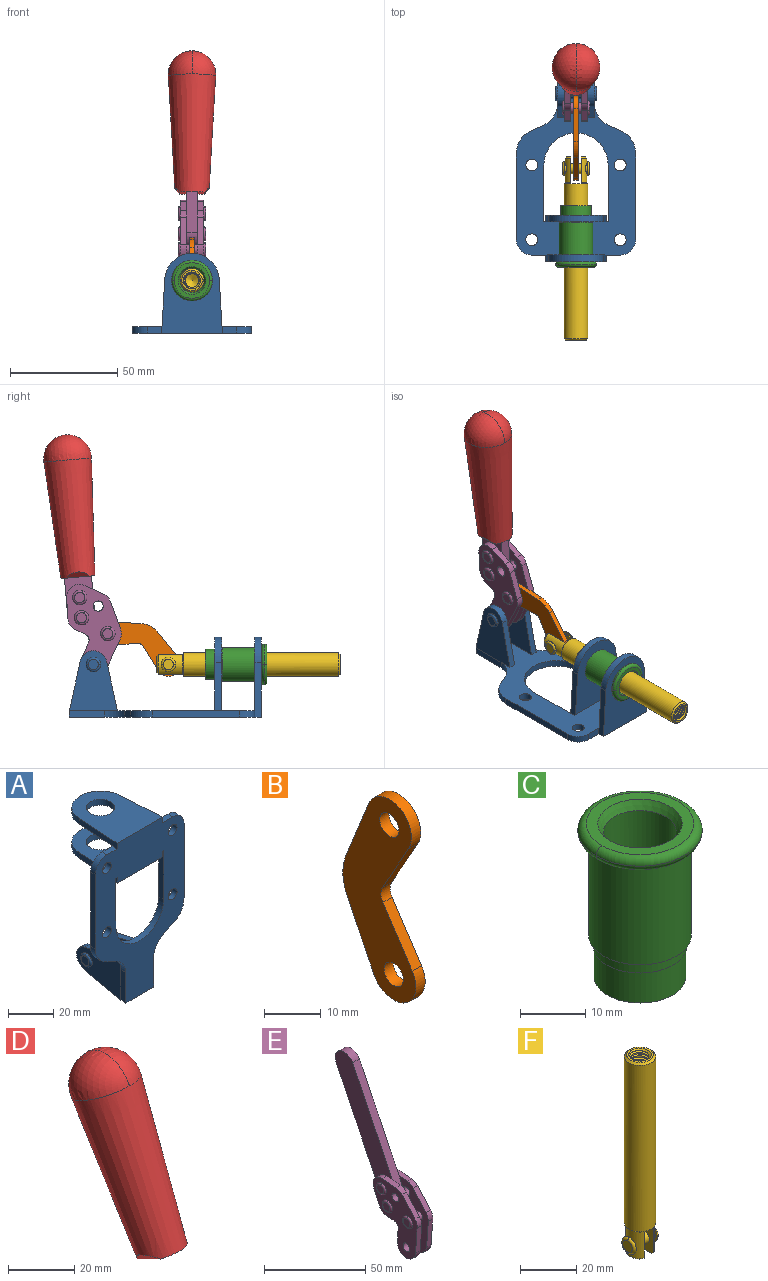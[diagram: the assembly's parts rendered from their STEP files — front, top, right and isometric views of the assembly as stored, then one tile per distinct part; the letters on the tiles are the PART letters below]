
ASSEMBLY  parts=6 mates=6
PART A: 55 faces, bbox 55.7x37.4x89.8 mm
  f0: torus R=2.41mm, axis (-1,0,0), area 15mm2, adj f11,f15,f25
  f1: torus R=2.41mm, axis (-1,0,0), area 15mm2, adj f10,f12,f22
  f2: cylinder r=2.78mm len=5.56mm, axis (0,-1,0), area 54.2mm2, adj f30,f54
  f3: cylinder r=14.99mm len=29.97mm, axis (0,-1,0), area 145.9mm2, adj f30,f49,f53,f54
  f4: cylinder r=2.78mm len=5.56mm, axis (0,-1,0), area 54.2mm2, adj f30,f54
  f5: cylinder r=2.78mm len=5.56mm, axis (0,-1,0), area 54.2mm2, adj f30,f54
  f6: cylinder r=2.78mm len=5.56mm, axis (0,-1,0), area 54.2mm2, adj f30,f54
  f7: cylinder r=6.35mm len=12.7mm, axis (0,0,1), area 123.6mm2, adj f27,f51
  f8: cylinder r=6.35mm len=12.7mm, axis (0,0,-1), area 124.7mm2, adj f21,f35
  f9: cylinder r=2.41mm len=11.18mm, axis (-1,0,0), area 169.4mm2, adj f16,f19
  f10: plane 4.83x4.83mm, normal (1,0,0), area 18.3mm2, adj f1,f12
  f11: plane 4.83x4.83mm, normal (-1,0,0), area 18.3mm2, adj f0,f15
  f12: torus R=2.41mm, axis (-1,0,0), area 15mm2, adj f1,f10,f22
  f13: cylinder r=6.35mm len=12.41mm, axis (1,0,0), area 53.4mm2, adj f18,f19,f22,f23
  f14: cylinder r=6.35mm len=12.41mm, axis (-1,0,0), area 53.4mm2, adj f16,f17,f24,f25
  f15: torus R=2.41mm, axis (-1,0,0), area 15mm2, adj f0,f11,f25
  f16: plane 27.86x22.35mm, normal (1,0,0), area 425.4mm2, adj f9,f14,f17,f24,f30
  f17: plane 22.86x4.97mm, normal (0,0.21,0.98), area 72.5mm2, adj f14,f16,f25,f30
  f18: plane 22.86x4.97mm, normal (0,0.21,0.98), area 72.5mm2, adj f13,f19,f22,f30
  f19: plane 27.86x22.35mm, normal (-1,0,0), area 425.4mm2, adj f9,f13,f18,f23,f30
  f20: cylinder r=12.7mm len=25.35mm, axis (0,0,-1), area 119.8mm2, adj f21,f34,f35,f36
  f21: plane 34.21x28.07mm, normal (0,0,-1), area 702.4mm2, adj f8,f20,f30,f34,f36
  f22: plane 27.96x22.45mm, normal (1,0,0), area 407.2mm2, adj f1,f12,f13,f18,f23,f30,f42,f43
  f23: plane 22.86x4.97mm, normal (0,0.21,-0.98), area 72.5mm2, adj f13,f19,f22,f44
  f24: plane 22.86x4.97mm, normal (0,0.21,-0.98), area 72.5mm2, adj f14,f16,f25,f44
  f25: plane 27.86x22.35mm, normal (-1,0,0), area 407.1mm2, adj f0,f14,f15,f17,f24,f30,f45,f46
  f26: plane 3.1x0.95mm, normal (0,0,-1), area 2.7mm2, adj f30,f49,f50,f54
  f27: plane 34.21x28.07mm, normal (0,0,1), area 702.4mm2, adj f7,f28,f30,f50,f52
  f28: cylinder r=12.7mm len=25.35mm, axis (0,0,1), area 118.8mm2, adj f27,f50,f51,f52
  f29: plane 3.1x0.95mm, normal (0,0,-1), area 2.7mm2, adj f30,f52,f53,f54
  f30: plane 86.54x55.63mm, normal (0,1,0), area 2362.9mm2, adj f2,f3,f4,f5,f6,f16,f17,f18
  f31: plane 40.56x3.1mm, normal (-1,0,0), area 125.7mm2, adj f30,f32,f48,f54
  f32: cylinder r=7.11mm len=7.11mm, axis (0,-1,0), area 34.6mm2, adj f30,f31,f33,f54
  f33: plane 6.67x3.1mm, normal (0,0,1), area 20.4mm2, adj f30,f32,f34,f54
  f34: plane 25.39x3.13mm, normal (-1,0.06,0), area 79.5mm2, adj f20,f21,f33,f35,f54
  f35: plane 37.31x28.45mm, normal (0,0,1), area 789.9mm2, adj f8,f20,f34,f36,f54
  f36: plane 25.39x3.13mm, normal (1,0.06,0), area 79.5mm2, adj f20,f21,f35,f37,f54
  f37: plane 6.67x3.1mm, normal (0,0,1), area 20.4mm2, adj f30,f36,f38,f54
  f38: cylinder r=7.11mm len=7.11mm, axis (0,-1,0), area 34.6mm2, adj f30,f37,f39,f54
  f39: plane 40.56x3.1mm, normal (1,0,0), area 125.7mm2, adj f30,f38,f40,f54
  f40: cylinder r=11.18mm len=10.16mm, axis (0,-1,0), area 39.5mm2, adj f30,f39,f41,f54
  f41: plane 6.09x3.1mm, normal (0.42,0,-0.91), area 20.8mm2, adj f30,f40,f42,f54
  f42: cylinder r=11.18mm len=9.41mm, axis (0,-1,0), area 37.2mm2, adj f22,f30,f41,f43,f54
  f43: plane 16.5x3.1mm, normal (1,0,0), area 51.1mm2, adj f22,f42,f44,f54
  f44: plane 17.37x3.1mm, normal (0,0,-1), area 53.8mm2, adj f23,f24,f30,f43,f45,f54
  f45: plane 16.5x3.1mm, normal (-1,0,0), area 51.1mm2, adj f25,f44,f46,f54
  f46: cylinder r=11.18mm len=9.41mm, axis (0,-1,0), area 37.2mm2, adj f25,f30,f45,f47,f54
  f47: plane 6.09x3.1mm, normal (-0.42,0,-0.91), area 20.8mm2, adj f30,f46,f48,f54
  f48: cylinder r=11.18mm len=10.16mm, axis (0,-1,0), area 39.5mm2, adj f30,f31,f47,f54
  f49: plane 26.54x3.1mm, normal (-1,0,0), area 82.3mm2, adj f3,f26,f30,f54
  f50: plane 25.39x3.1mm, normal (1,0.06,0), area 78.8mm2, adj f26,f27,f28,f51,f54
  f51: plane 37.31x28.45mm, normal (0,0,-1), area 789.9mm2, adj f7,f28,f50,f52,f54
  f52: plane 25.39x3.1mm, normal (-1,0.06,0), area 78.8mm2, adj f27,f28,f29,f51,f54
  f53: plane 26.54x3.1mm, normal (1,0,0), area 82.3mm2, adj f3,f29,f30,f54
  f54: plane 89.66x55.63mm, normal (0,-1,0), area 2678.5mm2, adj f2,f3,f4,f5,f6,f26,f29,f31
PART B: 12 faces, bbox 2.3x18.2x42.8 mm
  f0: cylinder r=2.4mm len=4.8mm, axis (1,0,0), area 34.9mm2, adj f4,f11
  f1: cylinder r=10.41mm len=8.47mm, axis (1,0,0), area 20.2mm2, adj f4,f9,f10,f11
  f2: cylinder r=3.05mm len=3.16mm, axis (1,0,0), area 7.7mm2, adj f4,f6,f7,f11
  f3: cylinder r=2.4mm len=4.8mm, axis (1,0,0), area 34.9mm2, adj f4,f11
  f4: plane 42.81x18.23mm, normal (-1,0,0), area 414.1mm2, adj f0,f1,f2,f3,f5,f6,f7,f8
  f5: cylinder r=5.54mm len=10.67mm, axis (1,0,0), area 41.8mm2, adj f4,f6,f10,f11
  f6: plane 11.66x6.53mm, normal (0,-0.87,-0.49), area 30.9mm2, adj f2,f4,f5,f11
  f7: plane 11.17x7.33mm, normal (0,-0.84,0.55), area 30.9mm2, adj f2,f4,f8,f11
  f8: cylinder r=5.54mm len=10.51mm, axis (1,0,0), area 41.8mm2, adj f4,f7,f9,f11
  f9: plane 13.67x6.67mm, normal (0,0.9,-0.44), area 35.1mm2, adj f1,f4,f8,f11
  f10: plane 14.1x5.7mm, normal (0,0.93,0.37), area 35.1mm2, adj f1,f4,f5,f11
  f11: plane 42.81x18.23mm, normal (1,0,0), area 414.1mm2, adj f0,f1,f2,f3,f5,f6,f7,f8
PART C: 15 faces, bbox 20.6x20.6x28.7 mm
  f0: torus R=8.26mm, axis (0,0,1), area 56.8mm2, adj f1,f10,f12
  f1: torus R=8.26mm, axis (0,0,1), area 56.8mm2, adj f0,f6,f13
  f2: cylinder r=5.59mm len=25.91mm, axis (0,0,1), area 909.6mm2, adj f3,f4
  f3: cone r=6.86mm half-angle=45deg, axis (0,0,-1), area 70.2mm2, adj f2,f14
  f4: cone r=6.47mm half-angle=30deg, axis (0,0,1), area 66.7mm2, adj f2,f13
  f5: cylinder r=7.04mm len=14.07mm, axis (0,0,1), area 252.6mm2, adj f11,f14
  f6: torus R=8.26mm, axis (0,0,1), area 56.8mm2, adj f1,f12,f13
  f7: cylinder r=7.16mm len=14.33mm, axis (0,0,1), area 91.5mm2, adj f9,f11
  f8: cylinder r=7.86mm len=18.42mm, axis (0,0,1), area 909.6mm2, adj f9,f10
  f9: plane 15.72x15.72mm, normal (0,0,-1), area 33mm2, adj f7,f8
  f10: plane 16.51x16.51mm, normal (0,0,-1), area 19.9mm2, adj f0,f8,f12
  f11: plane 14.33x14.33mm, normal (0,0,-1), area 5.7mm2, adj f5,f7
  f12: torus R=8.26mm, axis (0,0,1), area 56.8mm2, adj f0,f6,f10
  f13: plane 16.51x16.51mm, normal (0,0,1), area 82.7mm2, adj f1,f4,f6
  f14: plane 14.07x14.07mm, normal (0,0,-1), area 7.8mm2, adj f3,f5
PART D: 11 faces, bbox 22.3x42.6x64.5 mm
  f0: sphere r=11.13mm, area 411.4mm2, adj f1,f8
  f1: cone r=11.11mm half-angle=3.3deg, axis (0,0.44,0.9), area 3251.8mm2, adj f0,f7,f8,f9,f10
  f2: cylinder r=6.16mm len=11.7mm, axis (1,0,0), area 89.5mm2, adj f3,f4,f5,f6
  f3: plane 60.23x36.75mm, normal (-1,0,0), area 763.6mm2, adj f2,f4,f6,f10
  f4: plane 51.37x25.05mm, normal (0,0.9,-0.44), area 264.2mm2, adj f2,f3,f5,f10
  f5: plane 60.23x36.75mm, normal (1,0,0), area 763.6mm2, adj f2,f4,f6,f10
  f6: plane 51.37x25.05mm, normal (0,-0.9,0.44), area 264.2mm2, adj f2,f3,f5,f10
  f7: plane 9.95x5.95mm, normal (0.71,-0.31,-0.64), area 25.8mm2, adj f1,f10
  f8: sphere r=11.13mm, area 411.4mm2, adj f0,f1
  f9: plane 9.95x5.95mm, normal (-0.71,-0.31,-0.64), area 25.8mm2, adj f1,f10
  f10: plane 14.27x11.38mm, normal (0,-0.44,-0.9), area 106.7mm2, adj f1,f3,f4,f5,f6,f7,f9
PART E: 59 faces, bbox 12.9x60.2x99.6 mm
  f0: torus R=2.39mm, axis (-1,0,0), area 14.9mm2, adj f20,f43,f51
  f1: torus R=2.39mm, axis (-1,0,0), area 14.9mm2, adj f19,f42,f51
  f2: torus R=2.39mm, axis (-1,0,0), area 14.9mm2, adj f18,f35,f51
  f3: torus R=2.39mm, axis (-1,0,0), area 14.9mm2, adj f14,f17,f23
  f4: torus R=2.39mm, axis (-1,0,0), area 14.9mm2, adj f13,f16,f23
  f5: torus R=2.39mm, axis (-1,0,0), area 14.9mm2, adj f12,f15,f23
  f6: cylinder r=2.39mm len=4.78mm, axis (1,0,0), area 46.5mm2, adj f48,f50,f51
  f7: cylinder r=2.39mm len=4.78mm, axis (1,0,0), area 46.5mm2, adj f50,f51
  f8: cylinder r=6.35mm len=12.68mm, axis (1,0,0), area 61.8mm2, adj f38,f39,f50,f51
  f9: cylinder r=2.39mm len=4.78mm, axis (-1,0,0), area 70.5mm2, adj f46,f50
  f10: cylinder r=2.39mm len=4.78mm, axis (-1,0,0), area 46.5mm2, adj f23,f45,f46
  f11: cylinder r=2.39mm len=4.78mm, axis (-1,0,0), area 46.5mm2, adj f23,f46
  f12: plane 4.78x4.78mm, normal (1,0,0), area 17.9mm2, adj f5,f15
  f13: plane 4.78x4.78mm, normal (1,0,0), area 17.9mm2, adj f4,f16
  f14: plane 4.78x4.78mm, normal (1,0,0), area 17.9mm2, adj f3,f17
  f15: torus R=2.39mm, axis (-1,0,0), area 14.9mm2, adj f5,f12,f23
  f16: torus R=2.39mm, axis (-1,0,0), area 14.9mm2, adj f4,f13,f23
  f17: torus R=2.39mm, axis (-1,0,0), area 14.9mm2, adj f3,f14,f23
  f18: plane 4.78x4.78mm, normal (-1,0,0), area 17.9mm2, adj f2,f35
  f19: plane 4.78x4.78mm, normal (-1,0,0), area 17.9mm2, adj f1,f42
  f20: plane 4.78x4.78mm, normal (-1,0,0), area 17.9mm2, adj f0,f43
  f21: plane 2.26x0.2mm, normal (1,0,0), area 0.2mm2, adj f31,f44
  f22: plane 2.26x0.2mm, normal (-1,0,0), area 0.2mm2, adj f41,f44
  f23: plane 39.37x30.77mm, normal (1,0,0), area 565.5mm2, adj f3,f4,f5,f10,f11,f15,f16,f17
  f24: cylinder r=6.1mm len=4.15mm, axis (-1,0,0), area 14.7mm2, adj f23,f25,f32,f46
  f25: plane 10.25x9.01mm, normal (0,-0.75,0.66), area 42.3mm2, adj f23,f24,f26,f46
  f26: cylinder r=6.35mm len=4.64mm, axis (-1,0,0), area 15.6mm2, adj f23,f25,f27,f46
  f27: plane 15.84x3.1mm, normal (0,-1,-0.07), area 49.2mm2, adj f23,f26,f28,f46
  f28: cylinder r=6.35mm len=12.68mm, axis (-1,0,0), area 61.8mm2, adj f23,f27,f29,f46
  f29: plane 8.11x3.1mm, normal (0,1,0.07), area 25.2mm2, adj f23,f28,f30,f46
  f30: cylinder r=3.05mm len=3.25mm, axis (-1,0,0), area 14.8mm2, adj f23,f29,f31,f46
  f31: plane 5.99x3.1mm, normal (0,0.07,-1), area 18.6mm2, adj f21,f23,f30,f44,f46
  f32: plane 9.5x3.1mm, normal (0,-0.07,1), area 29.5mm2, adj f23,f24,f33,f46,f47
  f33: cylinder r=6.1mm len=8.63mm, axis (-1,0,0), area 39.1mm2, adj f23,f32,f34,f47
  f34: plane 8.65x3.96mm, normal (0,0.91,-0.42), area 29.5mm2, adj f23,f33,f44,f47
  f35: torus R=2.39mm, axis (-1,0,0), area 14.9mm2, adj f2,f18,f51
  f36: plane 10.25x9.01mm, normal (0,-0.75,0.66), area 42.3mm2, adj f37,f49,f50,f51
  f37: cylinder r=6.35mm len=4.64mm, axis (1,0,0), area 15.6mm2, adj f36,f38,f50,f51
  f38: plane 15.84x3.1mm, normal (0,-1,-0.07), area 49.2mm2, adj f8,f37,f50,f51
  f39: plane 8.11x3.1mm, normal (0,1,0.07), area 25.2mm2, adj f8,f40,f50,f51
  f40: cylinder r=3.05mm len=3.25mm, axis (1,0,0), area 14.8mm2, adj f39,f41,f50,f51
  f41: plane 5.99x3.1mm, normal (0,0.07,-1), area 18.6mm2, adj f22,f40,f44,f50,f51
  f42: torus R=2.39mm, axis (-1,0,0), area 14.9mm2, adj f1,f19,f51
  f43: torus R=2.39mm, axis (-1,0,0), area 14.9mm2, adj f0,f20,f51
  f44: cylinder r=6.35mm len=12.12mm, axis (-1,0,0), area 128.9mm2, adj f21,f22,f23,f31,f34,f41,f46,f47
  f45: plane 2.65x1.35mm, normal (1,0,0), area 1mm2, adj f10,f55
  f46: plane 39.08x20.42mm, normal (-1,0,0), area 412.5mm2, adj f9,f10,f11,f24,f25,f26,f27,f28
  f47: plane 77.62x39.82mm, normal (1,0,0), area 850mm2, adj f32,f33,f34,f44,f53,f54,f55
  f48: plane 2.65x1.35mm, normal (-1,0,0), area 1mm2, adj f6,f55
  f49: cylinder r=6.1mm len=4.15mm, axis (1,0,0), area 14.7mm2, adj f36,f50,f51,f56
  f50: plane 39.08x20.42mm, normal (1,0,0), area 412.5mm2, adj f6,f7,f8,f9,f36,f37,f38,f39
  f51: plane 39.37x30.77mm, normal (-1,0,0), area 565.5mm2, adj f0,f1,f2,f6,f7,f8,f35,f36
  f52: plane 8.65x3.96mm, normal (0,0.91,-0.42), area 29.5mm2, adj f44,f51,f57,f58
  f53: plane 68.49x33.4mm, normal (0,0.9,-0.44), area 358.1mm2, adj f44,f47,f54,f58
  f54: cylinder r=6.35mm len=12.06mm, axis (1,0,0), area 93.7mm2, adj f47,f53,f55,f58
  f55: plane 68.49x33.4mm, normal (0,-0.9,0.44), area 358.1mm2, adj f44,f45,f46,f47,f48,f50,f54,f58
  f56: plane 9.5x3.1mm, normal (0,-0.07,1), area 29.5mm2, adj f49,f50,f51,f57,f58
  f57: cylinder r=6.1mm len=8.63mm, axis (1,0,0), area 39.1mm2, adj f51,f52,f56,f58
  f58: plane 77.62x39.82mm, normal (-1,0,0), area 850mm2, adj f44,f52,f53,f54,f55,f56,f57
PART F: 48 faces, bbox 12.6x11.1x86.1 mm
  f0: torus R=2.41mm, axis (-1,0,0), area 15mm2, adj f30,f32,f34
  f1: torus R=2.41mm, axis (-1,0,0), area 15mm2, adj f29,f31,f33
  f2: cylinder r=5.54mm len=72.39mm, axis (0,0,1), area 2518.5mm2, adj f3,f4,f42,f43
  f3: cone r=5.54mm half-angle=45deg, axis (0,0,1), area 7.6mm2, adj f2,f5,f41
  f4: cone r=5.54mm half-angle=45deg, axis (0,0,-1), area 34.9mm2, adj f2,f39
  f5: cylinder r=5.08mm len=11.48mm, axis (0,0,1), area 108.3mm2, adj f3,f7,f8,f41
  f6: cylinder r=2.41mm len=4.83mm, axis (-1,0,0), area 71.2mm2, adj f40,f41
  f7: cylinder r=2.41mm len=4.83mm, axis (-1,0,0), area 7.6mm2, adj f5,f34
  f8: cone r=5.08mm half-angle=45deg, axis (0,0,1), area 10.6mm2, adj f5,f37,f41
  f9: cone r=3.98mm half-angle=45deg, axis (0,0,1), area 17.6mm2, adj f27,f39,f45,f46,f47
  f10: cylinder r=2.41mm len=4.83mm, axis (-1,0,0), area 7.6mm2, adj f33,f38
  f11: cylinder r=3.2mm len=6.4mm, axis (0,0,1), area 78.4mm2, adj f12,f28,f44,f45,f47
  f12: cylinder r=3.2mm len=6.4mm, axis (0,0,1), area 10.5mm2, adj f11,f13,f45,f47
  f13: cylinder r=3.2mm len=6.4mm, axis (0,0,1), area 10.5mm2, adj f12,f14,f45,f47
  f14: cylinder r=3.2mm len=6.4mm, axis (0,0,1), area 10.5mm2, adj f13,f15,f45,f47
  f15: cylinder r=3.2mm len=6.4mm, axis (0,0,1), area 10.5mm2, adj f14,f16,f45,f47
  f16: cylinder r=3.2mm len=6.4mm, axis (0,0,1), area 10.5mm2, adj f15,f17,f45,f47
  f17: cylinder r=3.2mm len=6.4mm, axis (0,0,1), area 10.5mm2, adj f16,f18,f45,f47
  f18: cylinder r=3.2mm len=6.4mm, axis (0,0,1), area 10.5mm2, adj f17,f19,f45,f47
  f19: cylinder r=3.2mm len=6.4mm, axis (0,0,1), area 10.5mm2, adj f18,f20,f45,f47
  f20: cylinder r=3.2mm len=6.4mm, axis (0,0,1), area 10.5mm2, adj f19,f21,f45,f47
  f21: cylinder r=3.2mm len=6.4mm, axis (0,0,1), area 10.5mm2, adj f20,f22,f45,f47
  f22: cylinder r=3.2mm len=6.4mm, axis (0,0,1), area 10.5mm2, adj f21,f23,f45,f47
  f23: cylinder r=3.2mm len=6.4mm, axis (0,0,1), area 10.5mm2, adj f22,f24,f45,f47
  f24: cylinder r=3.2mm len=6.4mm, axis (0,0,1), area 10.5mm2, adj f23,f25,f45,f47
  f25: cylinder r=3.2mm len=6.4mm, axis (0,0,1), area 10.5mm2, adj f24,f26,f45,f47
  f26: cylinder r=3.2mm len=6.4mm, axis (0,0,1), area 10.5mm2, adj f25,f27,f45,f47
  f27: cylinder r=3.2mm len=6.4mm, axis (0,0,1), area 7.4mm2, adj f9,f26,f45,f47
  f28: cone r=3.2mm half-angle=60deg, axis (0,0,1), area 37.2mm2, adj f11
  f29: plane 4.83x4.83mm, normal (-1,0,0), area 18.3mm2, adj f1,f31
  f30: plane 4.83x4.83mm, normal (1,0,0), area 18.3mm2, adj f0,f32
  f31: torus R=2.41mm, axis (-1,0,0), area 15mm2, adj f1,f29,f33
  f32: torus R=2.41mm, axis (-1,0,0), area 15mm2, adj f0,f30,f34
  f33: plane 6.83x6.83mm, normal (1,0,0), area 18.3mm2, adj f1,f10,f31
  f34: plane 6.83x6.83mm, normal (-1,0,0), area 18.3mm2, adj f0,f7,f32
  f35: cone r=5.08mm half-angle=45deg, axis (0,0,1), area 10.6mm2, adj f36,f38,f40
  f36: plane 7.25x1.97mm, normal (0,0,-1), area 10mm2, adj f35,f40
  f37: plane 7.25x1.97mm, normal (0,0,-1), area 10mm2, adj f8,f41
  f38: cylinder r=5.08mm len=11.48mm, axis (0,0,1), area 108.3mm2, adj f10,f35,f40,f42
  f39: plane 9.55x9.55mm, normal (0,0,1), area 22mm2, adj f4,f9
  f40: plane 12.76x10.09mm, normal (1,0,0), area 95.7mm2, adj f6,f35,f36,f38,f42,f43
  f41: plane 12.76x10.09mm, normal (-1,0,0), area 95.7mm2, adj f3,f5,f6,f8,f37,f43
  f42: cone r=5.54mm half-angle=45deg, axis (0,0,1), area 7.6mm2, adj f2,f38,f40
  f43: plane 11.07x4.7mm, normal (0,0,-1), area 50.4mm2, adj f2,f40,f41
  f44: plane 0.89x0.62mm, normal (-1,0,0), area 0.3mm2, adj f11,f45,f46,f47
  f45: bspline ~24.8x7.63mm, area 266.6mm2, adj f9,f11,f12,f13,f14,f15,f16,f17
  f46: bspline ~24.87x7.63mm, area 73.6mm2, adj f9,f44,f45,f47
  f47: bspline ~24.98x7.63mm, area 272.5mm2, adj f9,f11,f12,f13,f14,f15,f16,f17
PLACE A rot(axis=(1,0,0),90deg) t=(0,9.43,0)mm fixed
PLACE B rot(axis=(1,0,0),118.9deg) t=(0,31.96,10.56)mm
PLACE C rot(axis=(1,0,0),90deg) t=(0,9.43,0)mm
PLACE D rot(axis=(1,0,0),21deg) t=(0,7.04,45.75)mm
PLACE E rot(axis=(1,0,0),21deg) t=(0,7.04,45.75)mm
PLACE F rot(axis=(1,0,0),90deg) t=(0,21.98,0)mm
MATE fastened E.f54 <-> D.f2  axis (1,0,0) through (0,53.74,122.35)mm
MATE slider F.f2 <-> A.f7  axis (0,-1,0) through (0,-36.8,24.61)mm
MATE fastened C.f0 <-> A.f7  axis (0,1,0) through (0,-36.96,24.61)mm
MATE revolute B.f5 <-> F.f6  axis (1,0,0) through (0,6.51,24.61)mm
MATE revolute B.f3 <-> E.f4  axis (1,0,0) through (0,34.81,39)mm
MATE revolute A.f0 <-> E.f7  axis (-1,0,0) through (0,41.52,24.61)mm
